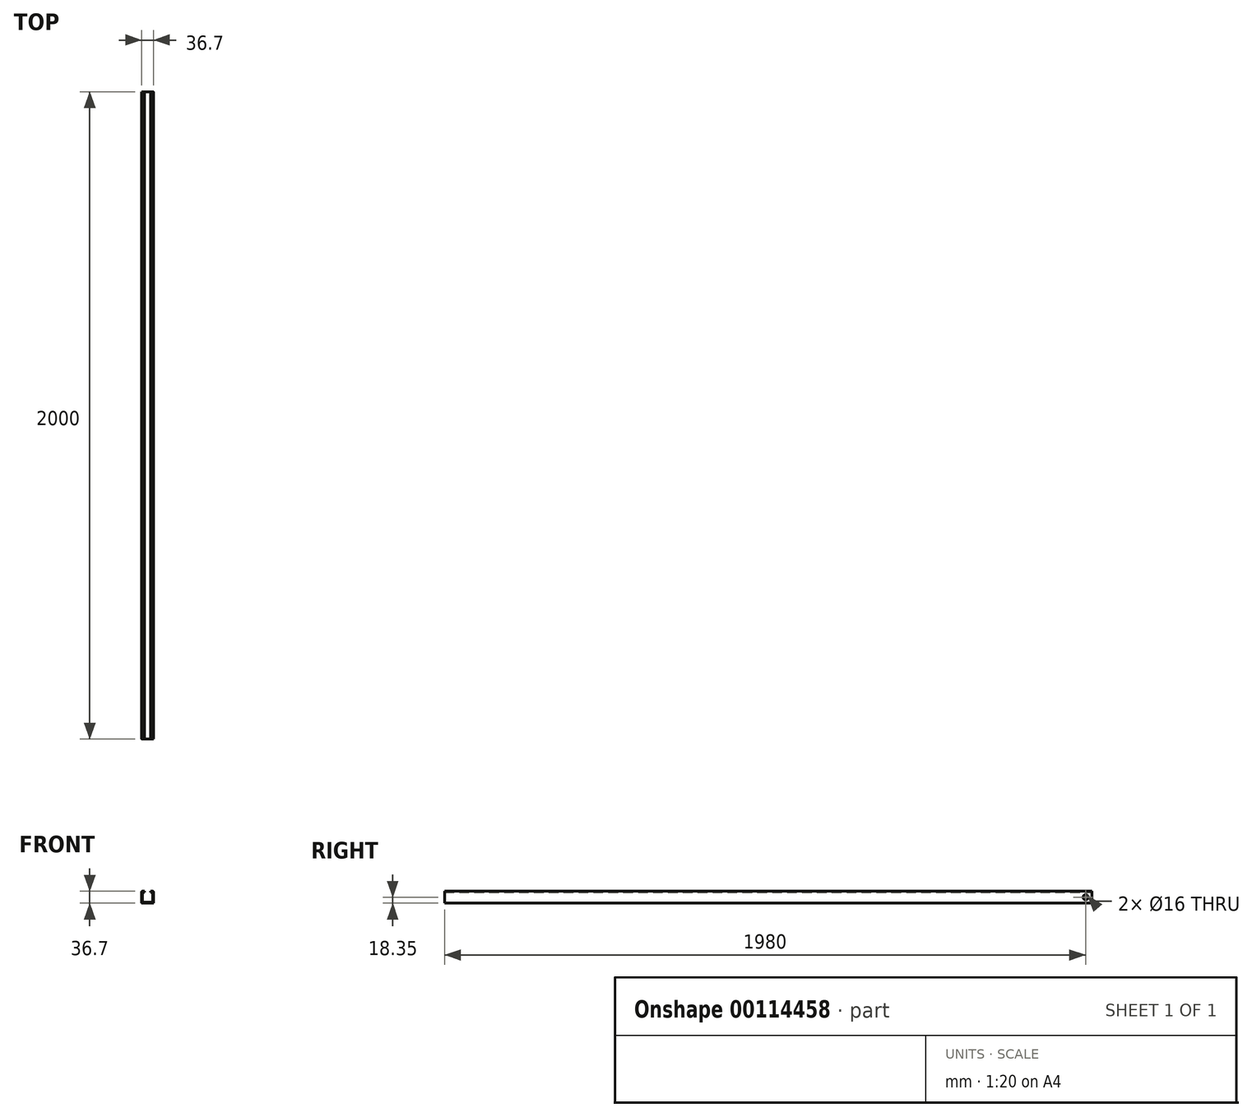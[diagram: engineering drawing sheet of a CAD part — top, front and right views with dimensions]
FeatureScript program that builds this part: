
annotation { "Feature Type Name" : "Feature", "Feature Type Description" : "" }
export const myFeature = defineFeature(function(context is Context, id is Id, definition is map)
    precondition{}
    {
        {
            var Q0;
            Q0=qCreatedBy(makeId("Front.planeOp"),FACE);
            var sketch = newSketch(context, id + "F0", { "sketchPlane" : qUnion([Q0])});
            skLineSegment(sketch, "E0.bottom", {"start": v(15.35, -15.35) * mm, "end": v(-15.35, -15.35) * mm});
            skLineSegment(sketch, "E0.top", {"start": v(15.35, 15.35) * mm, "end": v(9, 15.35) * mm});
            skLineSegment(sketch, "E0.left", {"start": v(15.35, -15.35) * mm, "end": v(15.35, 15.35) * mm});
            skLineSegment(sketch, "E0.right", {"start": v(-15.35, -15.35) * mm, "end": v(-15.35, 15.35) * mm});
            skPoint(sketch, "E0.middle", {"position": v(0, 0) * mm});
            skLineSegment(sketch, "E1.0", {"start": v(-18.35, -16.85) * mm, "end": v(-18.35, 16.85) * mm});
            skLineSegment(sketch, "E1.1", {"start": v(16.85, -18.35) * mm, "end": v(-16.85, -18.35) * mm});
            skLineSegment(sketch, "E1.2", {"start": v(18.35, -16.85) * mm, "end": v(18.35, 16.85) * mm});
            skLineSegment(sketch, "E1.3", {"start": v(16.85, 18.35) * mm, "end": v(9, 18.35) * mm});
            skPoint(sketch, "E2.visualSharp", {"position": v(-18.35, 18.35) * mm});
            skArc(sketch, "E2.filletArc", {"start": v(-16.85, 18.35) * mm, "mid": v(-17.91, 17.91) * mm, "end": v(-18.35, 16.85) * mm});
            skPoint(sketch, "E3.visualSharp", {"position": v(18.35, 18.35) * mm});
            skArc(sketch, "E3.filletArc", {"start": v(18.35, 16.85) * mm, "mid": v(17.91, 17.91) * mm, "end": v(16.85, 18.35) * mm});
            skPoint(sketch, "E4.visualSharp", {"position": v(18.35, -18.35) * mm});
            skArc(sketch, "E4.filletArc", {"start": v(16.85, -18.35) * mm, "mid": v(17.91, -17.91) * mm, "end": v(18.35, -16.85) * mm});
            skPoint(sketch, "E5.visualSharp", {"position": v(-18.35, -18.35) * mm});
            skArc(sketch, "E5.filletArc", {"start": v(-18.35, -16.85) * mm, "mid": v(-17.91, -17.91) * mm, "end": v(-16.85, -18.35) * mm});
            skLineSegment(sketch, "E6", {"start": v(-9, 18.35) * mm, "end": v(-9, 15.35) * mm});
            skLineSegment(sketch, "E7", {"start": v(-9, 15.35) * mm, "end": v(-9, 18.35) * mm});
            skLineSegment(sketch, "E8", {"start": v(9, 18.35) * mm, "end": v(9, 15.35) * mm});
            skLineSegment(sketch, "E9.trimOffspring", {"start": v(-9, 18.35) * mm, "end": v(-16.85, 18.35) * mm});
            skLineSegment(sketch, "E10.trimOffspring", {"start": v(-9, 15.35) * mm, "end": v(-15.35, 15.35) * mm});
            skSolve(sketch);
        }
        {
            var Q0;
            Q0=makeQuery(id+"F0.imprint","IMPRINT",FACE,{"disambiguationData":[TD([[makeQuery(id+"F0.imprint","IMPRINT",EDGE,{"derivedFrom":sQuery(id+"F0.wireOp",EDGE,"E0.bottom")}),1.0]])]});
            extrude(context, id + "F1", {"entities" : qUnion([Q0]), "depth" : 2000 * mm});
        }
        {
            var Q0;
            Q0=makeQuery(id+"F1.opExtrude","SWEPT_FACE",FACE,{"disambiguationData":[OSD([sQuery(id+"F0.wireOp",EDGE,"E1.2")])]});
            var sketch = newSketch(context, id + "F2", { "sketchPlane" : qUnion([Q0])});
            skCircle(sketch, "E11", {"center": v(-20, 0) * mm, "radius": 8 * mm});
            skSolve(sketch);
        }
        {
            var Q0;
            Q0=makeQuery(id+"F2.imprint","IMPRINT",FACE,{"disambiguationData":[TD([[makeQuery(id+"F2.imprint","IMPRINT",EDGE,{"derivedFrom":sQuery(id+"F2.wireOp",EDGE,"E11")}),1.0]])]});
            extrude(context, id + "F3", {"entities" : qUnion([Q0]), "operationType" : NewBodyOperationType.REMOVE, "endBound" : BoundingType.THROUGH_ALL, "oppositeDirection" : true, "depth" : 25 * mm});
        }
    });
